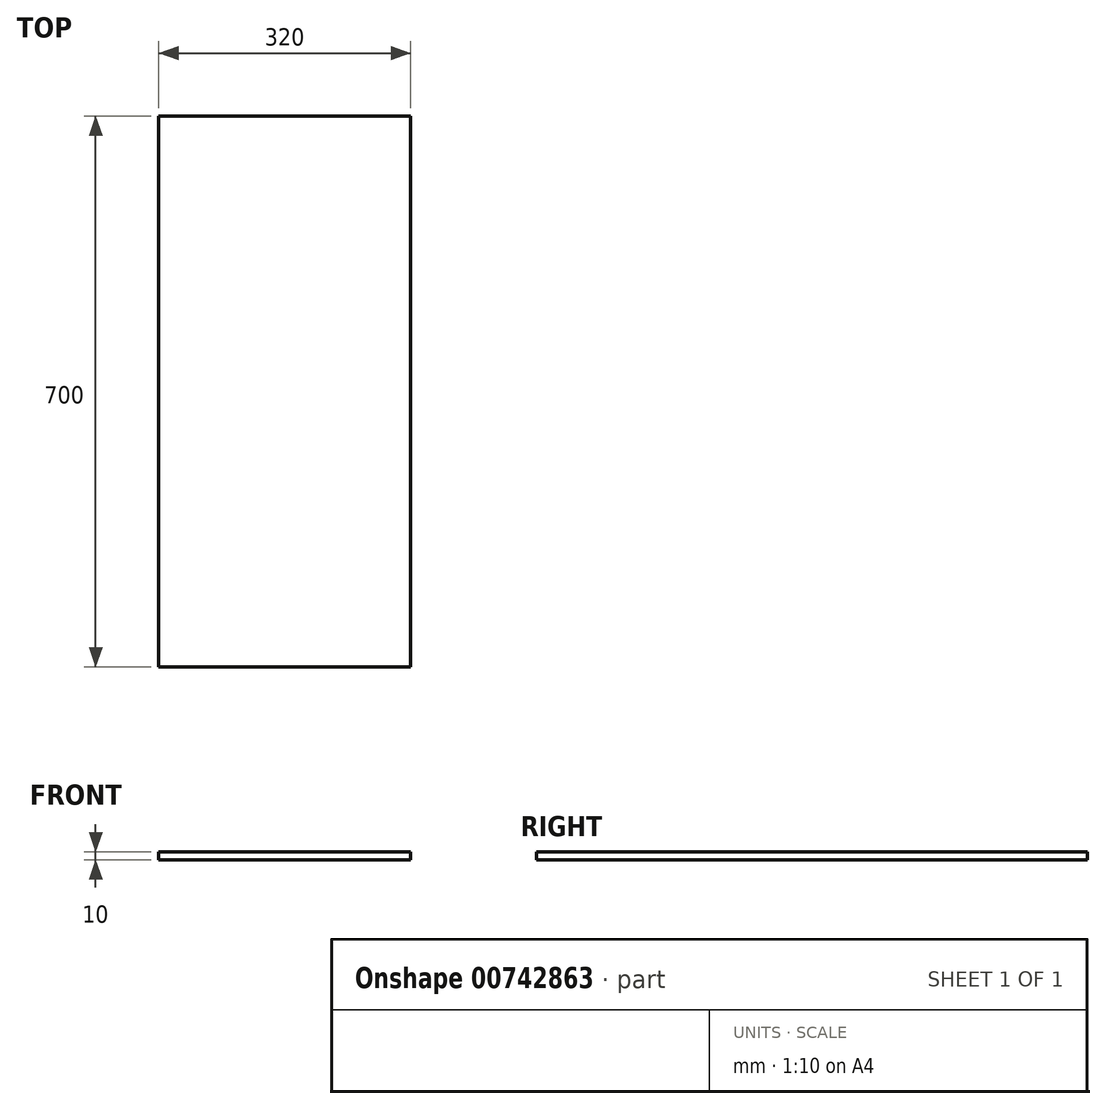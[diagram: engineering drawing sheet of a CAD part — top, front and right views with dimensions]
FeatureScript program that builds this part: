
annotation { "Feature Type Name" : "Feature", "Feature Type Description" : "" }
export const myFeature = defineFeature(function(context is Context, id is Id, definition is map)
    precondition{}
    {
        {
            var Q0;
            Q0=qCreatedBy(makeId("Top.planeOp"),FACE);
            var sketch = newSketch(context, id + "F0", { "sketchPlane" : qUnion([Q0])});
            skLineSegment(sketch, "E0.bottom", {"start": v(160, 350) * mm, "end": v(-160, 350) * mm});
            skLineSegment(sketch, "E0.top", {"start": v(160, -350) * mm, "end": v(-160, -350) * mm});
            skLineSegment(sketch, "E0.left", {"start": v(160, 350) * mm, "end": v(160, -350) * mm});
            skLineSegment(sketch, "E0.right", {"start": v(-160, 350) * mm, "end": v(-160, -350) * mm});
            skPoint(sketch, "E0.middle", {"position": v(0, 0) * mm});
            skSolve(sketch);
        }
        {
            var Q0;
            Q0 = qSketchRegion(id + "F0", true);
            extrude(context, id + "F1", {"entities" : qUnion([Q0]), "depth" : 10 * mm, "offsetDistance" : 25.4 * mm});
        }
    });
